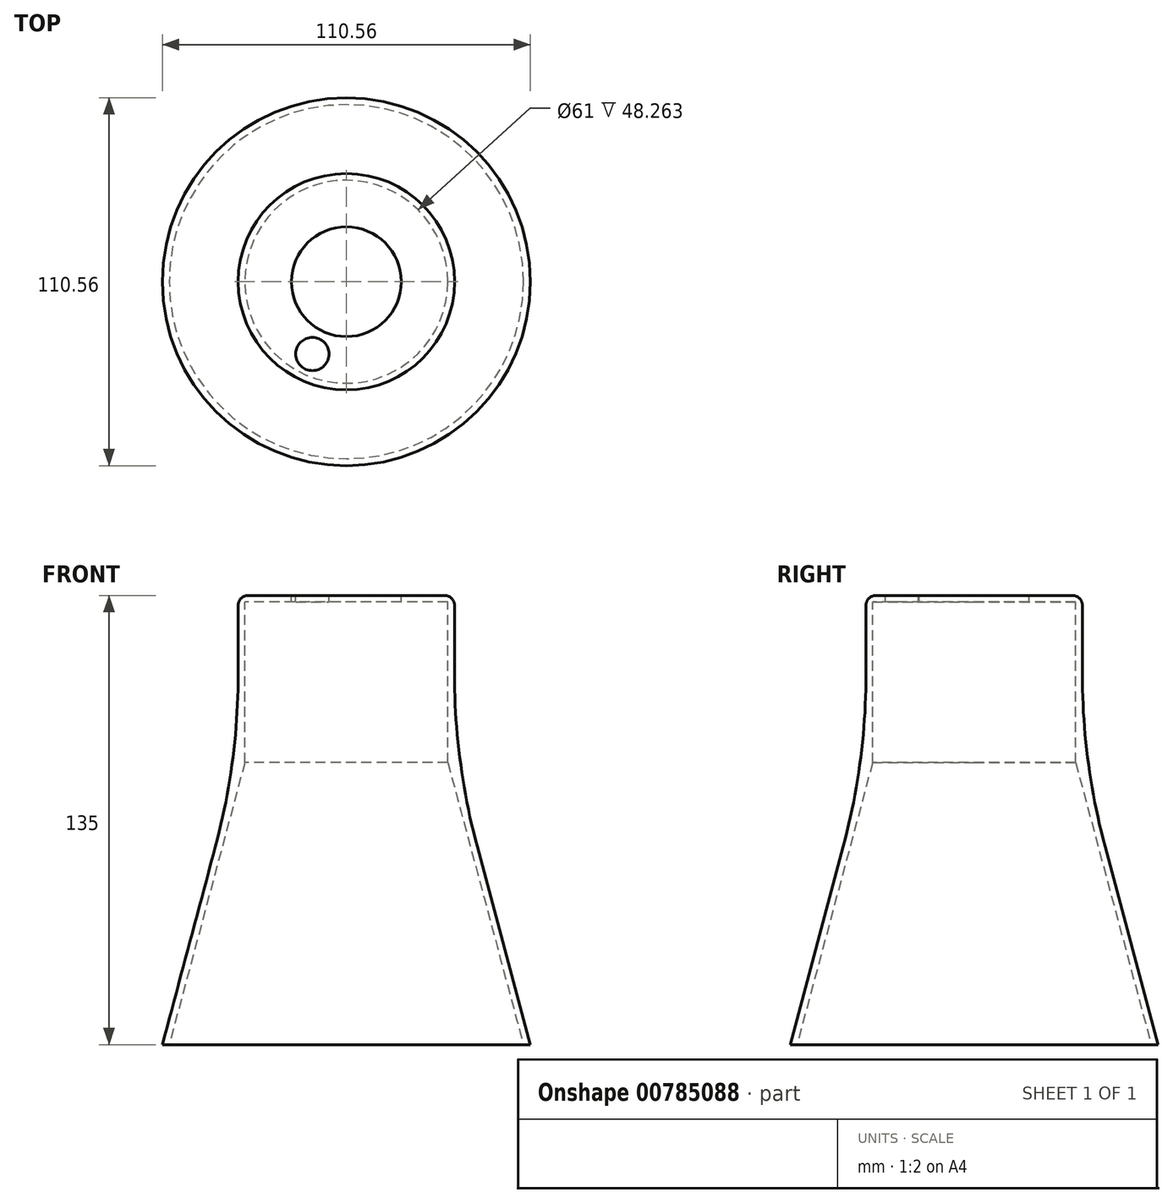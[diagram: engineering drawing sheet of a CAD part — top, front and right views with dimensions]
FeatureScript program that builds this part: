
annotation { "Feature Type Name" : "Feature", "Feature Type Description" : "" }
export const myFeature = defineFeature(function(context is Context, id is Id, definition is map)
    precondition{}
    {
        {
            var Q0;
            Q0=qCreatedBy(makeId("Front.planeOp"),FACE);
            var sketch = newSketch(context, id + "F0", { "sketchPlane" : qUnion([Q0])});
            skLineSegment(sketch, "E0", {"start": v(0, 164.24) * mm, "end": v(0, 0) * mm, "construction": true});
            skLineSegment(sketch, "E1", {"start": v(-16.5, 135) * mm, "end": v(-32.5, 135) * mm});
            skLineSegment(sketch, "E2", {"start": v(-32.5, 135) * mm, "end": v(-32.5, 85) * mm});
            skLineSegment(sketch, "E3", {"start": v(-32.5, 85) * mm, "end": v(-55.28, 0) * mm});
            skLineSegment(sketch, "E4", {"start": v(-55.28, 0) * mm, "end": v(-53.2, 0) * mm});
            skLineSegment(sketch, "E5", {"start": v(-53.2, 0) * mm, "end": v(-30.5, 84.74) * mm});
            skLineSegment(sketch, "E6", {"start": v(-30.5, 84.74) * mm, "end": v(-30.5, 133) * mm});
            skLineSegment(sketch, "E7", {"start": v(-30.5, 133) * mm, "end": v(-16.5, 133) * mm});
            skLineSegment(sketch, "E8", {"start": v(-16.5, 133) * mm, "end": v(-16.5, 135) * mm});
            skSolve(sketch);
        }
        {
            var Q0;
            Q0 = qSketchRegion(id + "F0", true);
            var Q1;
            Q1 = qConstructionFilter(qBodyType(qCreatedBy(id + "F0" ,EDGE), BodyType.WIRE), ConstructionObject.NO);
            var Q2;
            Q2=sQuery(id+"F0.wireOp",EDGE,"E0");
            revolve(context, id + "F1", {"surfaceOperationType" : NewSurfaceOperationType.NEW, "entities" : qUnion([Q0]), "surfaceEntities" : qUnion([Q1]), "axis" : qUnion([Q2]), "revolveType" : RevolveType.FULL});
        }
        {
            var Q0;
            Q0=makeQuery(id+"F1.opRevolve","SWEPT_EDGE",EDGE,{"disambiguationData":[OSD([sQuery(id+"F0.wireOp",EDGE,"E1"),sQuery(id+"F0.wireOp",EDGE,"E2")])]});
            fillet(context, id + "F2", {"entities" : qUnion([Q0]), "radius" : 3 * mm, "tangentPropagation" : true, "allowEdgeOverflow" : false});
        }
        {
            var Q0;
            Q0=makeQuery(id+"F1.opRevolve","SWEPT_EDGE",EDGE,{"disambiguationData":[OSD([sQuery(id+"F0.wireOp",EDGE,"E2"),sQuery(id+"F0.wireOp",EDGE,"E3")])]});
            fillet(context, id + "F3", {"entities" : qUnion([Q0]), "radius" : 200 * mm, "tangentPropagation" : true, "allowEdgeOverflow" : false});
        }
        {
            var Q0;
            Q0=makeQuery(id+"F1.opRevolve","SWEPT_FACE",FACE,{"disambiguationData":[OSD([sQuery(id+"F0.wireOp",EDGE,"E1")])]});
            var sketch = newSketch(context, id + "F4", { "sketchPlane" : qUnion([Q0])});
            skPoint(sketch, "E9", {"position": v(-10.2, -21.72) * mm});
            skSolve(sketch);
        }
        {
            var Q0;
            Q0=sQuery(id+"F4.wireOp",VERTEX,"E9");
            var Q1;
            Q1=makeQuery(id+"F1.opRevolve","SWEPT_BODY",BODY,{"disambiguationData":[OSD([sQuery(id+"F0.wireOp",EDGE,"E1"),sQuery(id+"F0.wireOp",EDGE,"E2"),sQuery(id+"F0.wireOp",EDGE,"E3"),sQuery(id+"F0.wireOp",EDGE,"E4"),sQuery(id+"F0.wireOp",EDGE,"E5"),sQuery(id+"F0.wireOp",EDGE,"E6"),sQuery(id+"F0.wireOp",EDGE,"E7"),sQuery(id+"F0.wireOp",EDGE,"E8")])]});
            hole(context, id + "F5", {"style" : HoleStyle.SIMPLE, "endStyle" : HoleEndStyle.THROUGH, "holeDiameter" : 10 * mm, "majorDiameter" : 5 * mm, "isTappedThrough" : true, "tappedDepth" : 12 * mm, "tapClearance" : 0, "startFromSketch" : true, "locations" : qUnion([Q0]), "scope" : qUnion([Q1])});
        }
    });
